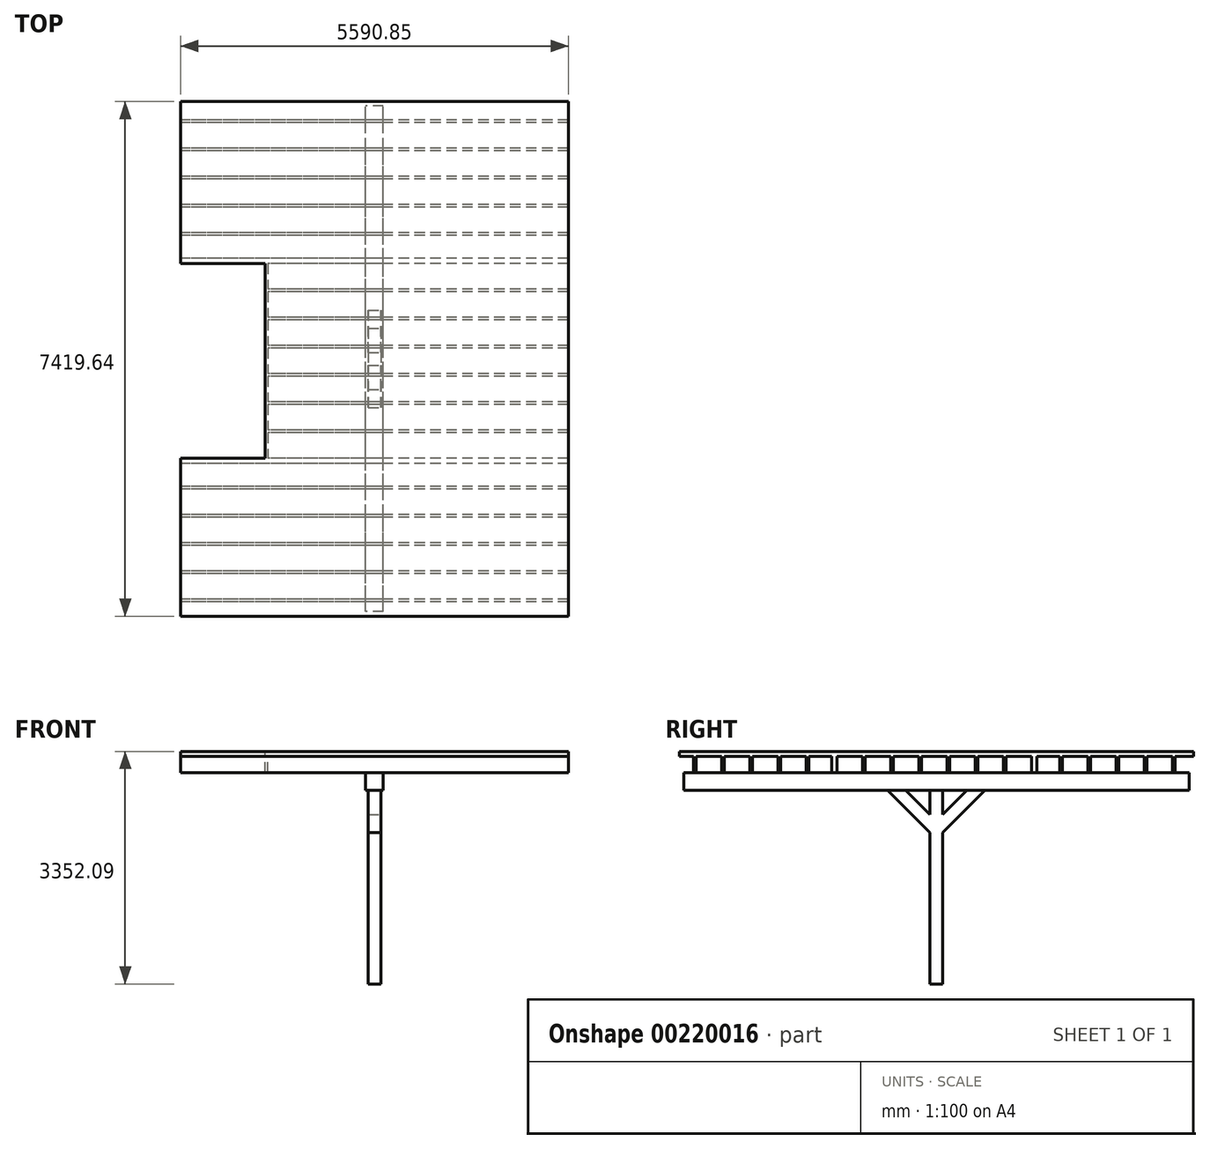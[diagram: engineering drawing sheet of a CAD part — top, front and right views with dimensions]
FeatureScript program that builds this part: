
annotation { "Feature Type Name" : "Feature", "Feature Type Description" : "" }
export const myFeature = defineFeature(function(context is Context, id is Id, definition is map)
    precondition{}
    {
        {
            var Q0;
            Q0=qCreatedBy(makeId("Top.planeOp"),FACE);
            var sketch = newSketch(context, id + "F0", { "sketchPlane" : qUnion([Q0])});
            skLineSegment(sketch, "E0.bottom", {"start": v(-4.2, 0) * mm, "end": v(5863.2, 0) * mm});
            skLineSegment(sketch, "E0.top", {"start": v(-4.2, -7696.2) * mm, "end": v(5863.2, -7696.2) * mm});
            skLineSegment(sketch, "E0.left", {"start": v(-4.2, 0) * mm, "end": v(-4.2, -7696.2) * mm});
            skLineSegment(sketch, "E0.right", {"start": v(5863.2, 0) * mm, "end": v(5863.2, -7696.2) * mm});
            skSolve(sketch);
        }
        {
            var Q0;
            Q0=makeQuery(id+"F0.imprint","IMPRINT",FACE,{"disambiguationData":[TD([[makeQuery(id+"F0.imprint","IMPRINT",EDGE,{"derivedFrom":sQuery(id+"F0.wireOp",EDGE,"E0.bottom")}),-1.0]])]});
            extrude(context, id + "F1", {"entities" : qUnion([Q0]), "depth" : 69.14 * mm});
        }
        {
            var Q0;
            Q0=makeQuery(id+"F1.opExtrude","CAP_FACE",FACE,{"disambiguationData":[OSD([sQuery(id+"F0.wireOp",EDGE,"E0.bottom"),sQuery(id+"F0.wireOp",EDGE,"E0.top"),sQuery(id+"F0.wireOp",EDGE,"E0.left"),sQuery(id+"F0.wireOp",EDGE,"E0.right")])],"isStart":true});
            var sketch = newSketch(context, id + "F2", { "sketchPlane" : qUnion([Q0])});
            skLineSegment(sketch, "E1.0", {"start": v(33.9, 7658.1) * mm, "end": v(5825.1, 7658.1) * mm});
            skLineSegment(sketch, "E1.1", {"start": v(33.9, 38.1) * mm, "end": v(33.9, 7658.1) * mm});
            skLineSegment(sketch, "E1.2", {"start": v(33.9, 38.1) * mm, "end": v(5825.1, 38.1) * mm});
            skLineSegment(sketch, "E1.3", {"start": v(5825.1, 38.1) * mm, "end": v(5825.1, 7658.1) * mm});
            skSolve(sketch);
        }
        {
            var Q0;
            Q0=makeQuery(id+"F2.imprint","IMPRINT",FACE,{"disambiguationData":[TD([[makeQuery(id+"F2.imprint","IMPRINT",EDGE,{"derivedFrom":sQuery(id+"F2.wireOp",EDGE,"E1.0")}),1.0]])]});
            extrude(context, id + "F3", {"entities" : qUnion([Q0]), "operationType" : NewBodyOperationType.ADD, "depth" : 234.95 * mm});
        }
        {
            var Q0;
            Q0=qCreatedBy(makeId("Right.planeOp"),FACE);
            var sketch = newSketch(context, id + "F4", { "sketchPlane" : qUnion([Q0])});
            skLineSegment(sketch, "E2.bottom", {"start": v(-406.4, 0) * mm, "end": v(-444.5, 0) * mm});
            skLineSegment(sketch, "E2.top", {"start": v(-406.4, -234.95) * mm, "end": v(-444.5, -234.95) * mm});
            skLineSegment(sketch, "E2.left", {"start": v(-406.4, 0) * mm, "end": v(-406.4, -234.95) * mm});
            skLineSegment(sketch, "E2.right", {"start": v(-444.5, 0) * mm, "end": v(-444.5, -234.95) * mm});
            skLineSegment(sketch, "E3.1.0.0", {"start": v(-812.8, 0) * mm, "end": v(-812.8, -234.95) * mm});
            skLineSegment(sketch, "E3.1.0.1", {"start": v(-850.9, 0) * mm, "end": v(-850.9, -234.95) * mm});
            skLineSegment(sketch, "E3.1.0.2", {"start": v(-812.8, 0) * mm, "end": v(-850.9, 0) * mm});
            skLineSegment(sketch, "E3.1.0.3", {"start": v(-812.8, -234.95) * mm, "end": v(-850.9, -234.95) * mm});
            skLineSegment(sketch, "E3.2.0.0", {"start": v(-1219.2, 0) * mm, "end": v(-1219.2, -234.95) * mm});
            skLineSegment(sketch, "E3.2.0.1", {"start": v(-1257.3, 0) * mm, "end": v(-1257.3, -234.95) * mm});
            skLineSegment(sketch, "E3.2.0.2", {"start": v(-1219.2, 0) * mm, "end": v(-1257.3, 0) * mm});
            skLineSegment(sketch, "E3.2.0.3", {"start": v(-1219.2, -234.95) * mm, "end": v(-1257.3, -234.95) * mm});
            skLineSegment(sketch, "E3.3.0.0", {"start": v(-1625.6, 0) * mm, "end": v(-1625.6, -234.95) * mm});
            skLineSegment(sketch, "E3.3.0.1", {"start": v(-1663.7, 0) * mm, "end": v(-1663.7, -234.95) * mm});
            skLineSegment(sketch, "E3.3.0.2", {"start": v(-1625.6, 0) * mm, "end": v(-1663.7, 0) * mm});
            skLineSegment(sketch, "E3.3.0.3", {"start": v(-1625.6, -234.95) * mm, "end": v(-1663.7, -234.95) * mm});
            skLineSegment(sketch, "E3.4.0.0", {"start": v(-2032, 0) * mm, "end": v(-2032, -234.95) * mm});
            skLineSegment(sketch, "E3.4.0.1", {"start": v(-2070.1, 0) * mm, "end": v(-2070.1, -234.95) * mm});
            skLineSegment(sketch, "E3.4.0.2", {"start": v(-2032, 0) * mm, "end": v(-2070.1, 0) * mm});
            skLineSegment(sketch, "E3.4.0.3", {"start": v(-2032, -234.95) * mm, "end": v(-2070.1, -234.95) * mm});
            skLineSegment(sketch, "E3.5.0.0", {"start": v(-2438.4, 0) * mm, "end": v(-2438.4, -234.95) * mm});
            skLineSegment(sketch, "E3.5.0.1", {"start": v(-2476.5, 0) * mm, "end": v(-2476.5, -234.95) * mm});
            skLineSegment(sketch, "E3.5.0.2", {"start": v(-2438.4, 0) * mm, "end": v(-2476.5, 0) * mm});
            skLineSegment(sketch, "E3.5.0.3", {"start": v(-2438.4, -234.95) * mm, "end": v(-2476.5, -234.95) * mm});
            skLineSegment(sketch, "E3.6.0.0", {"start": v(-2844.8, 0) * mm, "end": v(-2844.8, -234.95) * mm});
            skLineSegment(sketch, "E3.6.0.1", {"start": v(-2882.9, 0) * mm, "end": v(-2882.9, -234.95) * mm});
            skLineSegment(sketch, "E3.6.0.2", {"start": v(-2844.8, 0) * mm, "end": v(-2882.9, 0) * mm});
            skLineSegment(sketch, "E3.6.0.3", {"start": v(-2844.8, -234.95) * mm, "end": v(-2882.9, -234.95) * mm});
            skLineSegment(sketch, "E3.7.0.0", {"start": v(-3251.2, 0) * mm, "end": v(-3251.2, -234.95) * mm});
            skLineSegment(sketch, "E3.7.0.1", {"start": v(-3289.3, 0) * mm, "end": v(-3289.3, -234.95) * mm});
            skLineSegment(sketch, "E3.7.0.2", {"start": v(-3251.2, 0) * mm, "end": v(-3289.3, 0) * mm});
            skLineSegment(sketch, "E3.7.0.3", {"start": v(-3251.2, -234.95) * mm, "end": v(-3289.3, -234.95) * mm});
            skLineSegment(sketch, "E3.8.0.0", {"start": v(-3657.6, 0) * mm, "end": v(-3657.6, -234.95) * mm});
            skLineSegment(sketch, "E3.8.0.1", {"start": v(-3695.7, 0) * mm, "end": v(-3695.7, -234.95) * mm});
            skLineSegment(sketch, "E3.8.0.2", {"start": v(-3657.6, 0) * mm, "end": v(-3695.7, 0) * mm});
            skLineSegment(sketch, "E3.8.0.3", {"start": v(-3657.6, -234.95) * mm, "end": v(-3695.7, -234.95) * mm});
            skLineSegment(sketch, "E3.9.0.0", {"start": v(-4064, 0) * mm, "end": v(-4064, -234.95) * mm});
            skLineSegment(sketch, "E3.9.0.1", {"start": v(-4102.1, 0) * mm, "end": v(-4102.1, -234.95) * mm});
            skLineSegment(sketch, "E3.9.0.2", {"start": v(-4064, 0) * mm, "end": v(-4102.1, 0) * mm});
            skLineSegment(sketch, "E3.9.0.3", {"start": v(-4064, -234.95) * mm, "end": v(-4102.1, -234.95) * mm});
            skLineSegment(sketch, "E3.10.0.0", {"start": v(-4470.4, 0) * mm, "end": v(-4470.4, -234.95) * mm});
            skLineSegment(sketch, "E3.10.0.1", {"start": v(-4508.5, 0) * mm, "end": v(-4508.5, -234.95) * mm});
            skLineSegment(sketch, "E3.10.0.2", {"start": v(-4470.4, 0) * mm, "end": v(-4508.5, 0) * mm});
            skLineSegment(sketch, "E3.10.0.3", {"start": v(-4470.4, -234.95) * mm, "end": v(-4508.5, -234.95) * mm});
            skLineSegment(sketch, "E3.11.0.0", {"start": v(-4876.8, 0) * mm, "end": v(-4876.8, -234.95) * mm});
            skLineSegment(sketch, "E3.11.0.1", {"start": v(-4914.9, 0) * mm, "end": v(-4914.9, -234.95) * mm});
            skLineSegment(sketch, "E3.11.0.2", {"start": v(-4876.8, 0) * mm, "end": v(-4914.9, 0) * mm});
            skLineSegment(sketch, "E3.11.0.3", {"start": v(-4876.8, -234.95) * mm, "end": v(-4914.9, -234.95) * mm});
            skLineSegment(sketch, "E3.12.0.0", {"start": v(-5283.2, 0) * mm, "end": v(-5283.2, -234.95) * mm});
            skLineSegment(sketch, "E3.12.0.1", {"start": v(-5321.3, 0) * mm, "end": v(-5321.3, -234.95) * mm});
            skLineSegment(sketch, "E3.12.0.2", {"start": v(-5283.2, 0) * mm, "end": v(-5321.3, 0) * mm});
            skLineSegment(sketch, "E3.12.0.3", {"start": v(-5283.2, -234.95) * mm, "end": v(-5321.3, -234.95) * mm});
            skLineSegment(sketch, "E3.13.0.0", {"start": v(-5689.6, 0) * mm, "end": v(-5689.6, -234.95) * mm});
            skLineSegment(sketch, "E3.13.0.1", {"start": v(-5727.7, 0) * mm, "end": v(-5727.7, -234.95) * mm});
            skLineSegment(sketch, "E3.13.0.2", {"start": v(-5689.6, 0) * mm, "end": v(-5727.7, 0) * mm});
            skLineSegment(sketch, "E3.13.0.3", {"start": v(-5689.6, -234.95) * mm, "end": v(-5727.7, -234.95) * mm});
            skLineSegment(sketch, "E3.14.0.0", {"start": v(-6096, 0) * mm, "end": v(-6096, -234.95) * mm});
            skLineSegment(sketch, "E3.14.0.1", {"start": v(-6134.1, 0) * mm, "end": v(-6134.1, -234.95) * mm});
            skLineSegment(sketch, "E3.14.0.2", {"start": v(-6096, 0) * mm, "end": v(-6134.1, 0) * mm});
            skLineSegment(sketch, "E3.14.0.3", {"start": v(-6096, -234.95) * mm, "end": v(-6134.1, -234.95) * mm});
            skLineSegment(sketch, "E3.15.0.0", {"start": v(-6502.4, 0) * mm, "end": v(-6502.4, -234.95) * mm});
            skLineSegment(sketch, "E3.15.0.1", {"start": v(-6540.5, 0) * mm, "end": v(-6540.5, -234.95) * mm});
            skLineSegment(sketch, "E3.15.0.2", {"start": v(-6502.4, 0) * mm, "end": v(-6540.5, 0) * mm});
            skLineSegment(sketch, "E3.15.0.3", {"start": v(-6502.4, -234.95) * mm, "end": v(-6540.5, -234.95) * mm});
            skLineSegment(sketch, "E3.16.0.0", {"start": v(-6908.8, 0) * mm, "end": v(-6908.8, -234.95) * mm});
            skLineSegment(sketch, "E3.16.0.1", {"start": v(-6946.9, 0) * mm, "end": v(-6946.9, -234.95) * mm});
            skLineSegment(sketch, "E3.16.0.2", {"start": v(-6908.8, 0) * mm, "end": v(-6946.9, 0) * mm});
            skLineSegment(sketch, "E3.16.0.3", {"start": v(-6908.8, -234.95) * mm, "end": v(-6946.9, -234.95) * mm});
            skLineSegment(sketch, "E3.direction1", {"start": v(-444.5, -234.95) * mm, "end": v(-850.9, -234.95) * mm, "construction": true});
            skLineSegment(sketch, "E4.0.17.0", {"start": v(-7315.2, 0) * mm, "end": v(-7315.2, -234.95) * mm});
            skLineSegment(sketch, "E4.3.17.0", {"start": v(-7353.3, 0) * mm, "end": v(-7353.3, -234.95) * mm});
            skLineSegment(sketch, "E4.6.17.0", {"start": v(-7315.2, 0) * mm, "end": v(-7353.3, 0) * mm});
            skLineSegment(sketch, "E4.9.17.0", {"start": v(-7315.2, -234.95) * mm, "end": v(-7353.3, -234.95) * mm});
            skSolve(sketch);
        }
        {
            var Q0;
            Q0=makeQuery(id+"F4.imprint","IMPRINT",FACE,{"disambiguationData":[TD([[makeQuery(id+"F4.imprint","IMPRINT",EDGE,{"derivedFrom":sQuery(id+"F4.wireOp",EDGE,"E2.bottom")}),1.0]])]});
            var Q1;
            Q1=makeQuery(id+"F4.imprint","IMPRINT",FACE,{"disambiguationData":[TD([[makeQuery(id+"F4.imprint","IMPRINT",EDGE,{"derivedFrom":sQuery(id+"F4.wireOp",EDGE,"E3.1.0.0")}),-1.0]])]});
            var Q2;
            Q2=makeQuery(id+"F4.imprint","IMPRINT",FACE,{"disambiguationData":[TD([[makeQuery(id+"F4.imprint","IMPRINT",EDGE,{"derivedFrom":sQuery(id+"F4.wireOp",EDGE,"E3.2.0.0")}),-1.0]])]});
            var Q3;
            Q3=makeQuery(id+"F4.imprint","IMPRINT",FACE,{"disambiguationData":[TD([[makeQuery(id+"F4.imprint","IMPRINT",EDGE,{"derivedFrom":sQuery(id+"F4.wireOp",EDGE,"E3.3.0.0")}),-1.0]])]});
            var Q4;
            Q4=makeQuery(id+"F4.imprint","IMPRINT",FACE,{"disambiguationData":[TD([[makeQuery(id+"F4.imprint","IMPRINT",EDGE,{"derivedFrom":sQuery(id+"F4.wireOp",EDGE,"E3.4.0.0")}),-1.0]])]});
            var Q5;
            Q5=makeQuery(id+"F4.imprint","IMPRINT",FACE,{"disambiguationData":[TD([[makeQuery(id+"F4.imprint","IMPRINT",EDGE,{"derivedFrom":sQuery(id+"F4.wireOp",EDGE,"E3.5.0.0")}),-1.0]])]});
            var Q6;
            Q6=makeQuery(id+"F4.imprint","IMPRINT",FACE,{"disambiguationData":[TD([[makeQuery(id+"F4.imprint","IMPRINT",EDGE,{"derivedFrom":sQuery(id+"F4.wireOp",EDGE,"E3.6.0.0")}),-1.0]])]});
            var Q7;
            Q7=makeQuery(id+"F4.imprint","IMPRINT",FACE,{"disambiguationData":[TD([[makeQuery(id+"F4.imprint","IMPRINT",EDGE,{"derivedFrom":sQuery(id+"F4.wireOp",EDGE,"E3.7.0.0")}),-1.0]])]});
            var Q8;
            Q8=makeQuery(id+"F4.imprint","IMPRINT",FACE,{"disambiguationData":[TD([[makeQuery(id+"F4.imprint","IMPRINT",EDGE,{"derivedFrom":sQuery(id+"F4.wireOp",EDGE,"E3.8.0.0")}),-1.0]])]});
            var Q9;
            Q9=makeQuery(id+"F4.imprint","IMPRINT",FACE,{"disambiguationData":[TD([[makeQuery(id+"F4.imprint","IMPRINT",EDGE,{"derivedFrom":sQuery(id+"F4.wireOp",EDGE,"E3.9.0.0")}),-1.0]])]});
            var Q10;
            Q10=makeQuery(id+"F4.imprint","IMPRINT",FACE,{"disambiguationData":[TD([[makeQuery(id+"F4.imprint","IMPRINT",EDGE,{"derivedFrom":sQuery(id+"F4.wireOp",EDGE,"E3.10.0.0")}),-1.0]])]});
            var Q11;
            Q11=makeQuery(id+"F4.imprint","IMPRINT",FACE,{"disambiguationData":[TD([[makeQuery(id+"F4.imprint","IMPRINT",EDGE,{"derivedFrom":sQuery(id+"F4.wireOp",EDGE,"E3.11.0.0")}),-1.0]])]});
            var Q12;
            Q12=makeQuery(id+"F4.imprint","IMPRINT",FACE,{"disambiguationData":[TD([[makeQuery(id+"F4.imprint","IMPRINT",EDGE,{"derivedFrom":sQuery(id+"F4.wireOp",EDGE,"E3.12.0.0")}),-1.0]])]});
            var Q13;
            Q13=makeQuery(id+"F4.imprint","IMPRINT",FACE,{"disambiguationData":[TD([[makeQuery(id+"F4.imprint","IMPRINT",EDGE,{"derivedFrom":sQuery(id+"F4.wireOp",EDGE,"E3.13.0.0")}),-1.0]])]});
            var Q14;
            Q14=makeQuery(id+"F4.imprint","IMPRINT",FACE,{"disambiguationData":[TD([[makeQuery(id+"F4.imprint","IMPRINT",EDGE,{"derivedFrom":sQuery(id+"F4.wireOp",EDGE,"E3.14.0.0")}),-1.0]])]});
            var Q15;
            Q15=makeQuery(id+"F4.imprint","IMPRINT",FACE,{"disambiguationData":[TD([[makeQuery(id+"F4.imprint","IMPRINT",EDGE,{"derivedFrom":sQuery(id+"F4.wireOp",EDGE,"E3.15.0.0")}),-1.0]])]});
            var Q16;
            Q16=makeQuery(id+"F4.imprint","IMPRINT",FACE,{"disambiguationData":[TD([[makeQuery(id+"F4.imprint","IMPRINT",EDGE,{"derivedFrom":sQuery(id+"F4.wireOp",EDGE,"E3.16.0.0")}),-1.0]])]});
            var Q17;
            Q17=makeQuery(id+"F4.imprint","IMPRINT",FACE,{"disambiguationData":[TD([[makeQuery(id+"F4.imprint","IMPRINT",EDGE,{"derivedFrom":sQuery(id+"F4.wireOp",EDGE,"E4.0.17.0")}),-1.0]])]});
            var Q18;
            Q18=makeQuery(id+"F1.opExtrude","SWEPT_FACE",FACE,{"disambiguationData":[OSD([sQuery(id+"F0.wireOp",EDGE,"E0.right")])]});
            extrude(context, id + "F5", {"entities" : qUnion([Q0, Q1, Q2, Q3, Q4, Q5, Q6, Q7, Q8, Q9, Q10, Q11, Q12, Q13, Q14, Q15, Q16, Q17]), "operationType" : NewBodyOperationType.ADD, "endBound" : BoundingType.UP_TO_SURFACE, "endBoundEntityFace" : qUnion([Q18]), "depth" : 25.4 * mm});
        }
        {
            var Q0;
            {var subQ0=sQuery(id+"F0.wireOp",EDGE,"E0.bottom");Q0=makeQuery(id+"F3.boolean.opBoolean","MERGE",FACE,{"derivedFrom":[makeQuery(id+"F1.opExtrude","SWEPT_FACE",FACE,{"disambiguationData":[OSD([subQ0])]}),makeQuery(id+"F3.opExtrude","SWEPT_FACE",FACE,{"disambiguationData":[OSD([subQ0])]})]});}
            cPlane(context, id + "F6", {"entities" : qUnion([Q0]), "cplaneType" : CPlaneType.OFFSET, "offset" : 203.2 * mm, "oppositeDirection" : true, "width" : 152.4 * mm, "height" : 152.4 * mm});
        }
        {
            var Q0;
            Q0=qCreatedBy(id+"F6.planeOp",FACE);
            var sketch = newSketch(context, id + "F7", { "sketchPlane" : qUnion([Q0])});
            skLineSegment(sketch, "E5.bottom", {"start": v(-3056.5, -234.95) * mm, "end": v(-2802.5, -234.95) * mm});
            skLineSegment(sketch, "E5.top", {"start": v(-3056.5, -488.95) * mm, "end": v(-2802.5, -488.95) * mm});
            skLineSegment(sketch, "E5.left", {"start": v(-3056.5, -234.95) * mm, "end": v(-3056.5, -488.95) * mm});
            skLineSegment(sketch, "E5.right", {"start": v(-2802.5, -234.95) * mm, "end": v(-2802.5, -488.95) * mm});
            skSolve(sketch);
        }
        {
            var Q0;
            Q0=makeQuery(id+"F7.imprint","IMPRINT",FACE,{"disambiguationData":[TD([[makeQuery(id+"F7.imprint","IMPRINT",EDGE,{"derivedFrom":sQuery(id+"F7.wireOp",EDGE,"E5.bottom")}),-1.0]])]});
            extrude(context, id + "F8", {"entities" : qUnion([Q0]), "operationType" : NewBodyOperationType.ADD, "oppositeDirection" : true, "depth" : 7289.8 * mm});
        }
        {
            var Q0;
            Q0=makeQuery(id+"F8.opExtrude","SWEPT_FACE",FACE,{"disambiguationData":[OSD([sQuery(id+"F7.wireOp",EDGE,"E5.top")])]});
            var sketch = newSketch(context, id + "F9", { "sketchPlane" : qUnion([Q0])});
            skLineSegment(sketch, "E6", {"start": v(2929.5, 7493) * mm, "end": v(2929.5, 203.2) * mm, "construction": true});
            skLineSegment(sketch, "E7", {"start": v(2802.5, 3848.1) * mm, "end": v(3056.5, 3848.1) * mm, "construction": true});
            skLineSegment(sketch, "E8.bottom", {"start": v(3021.58, 3756.03) * mm, "end": v(2837.43, 3756.03) * mm});
            skLineSegment(sketch, "E8.top", {"start": v(3021.58, 3940.18) * mm, "end": v(2837.43, 3940.18) * mm});
            skLineSegment(sketch, "E8.left", {"start": v(3021.58, 3756.03) * mm, "end": v(3021.58, 3940.18) * mm});
            skLineSegment(sketch, "E8.right", {"start": v(2837.43, 3756.03) * mm, "end": v(2837.43, 3940.18) * mm});
            skPoint(sketch, "E8.middle", {"position": v(2929.5, 3848.1) * mm});
            skSolve(sketch);
        }
        {
            var Q0;
            Q0=makeQuery(id+"F9.imprint","IMPRINT",FACE,{"disambiguationData":[TD([[makeQuery(id+"F9.imprint","IMPRINT",EDGE,{"derivedFrom":sQuery(id+"F9.wireOp",EDGE,"E8.bottom")}),-1.0]])]});
            extrude(context, id + "F10", {"entities" : qUnion([Q0]), "operationType" : NewBodyOperationType.ADD, "depth" : 2794 * mm});
        }
        {
            var Q0;
            Q0=makeQuery(id+"F10.opExtrude","SWEPT_FACE",FACE,{"disambiguationData":[OSD([sQuery(id+"F9.wireOp",EDGE,"E8.left")])]});
            var sketch = newSketch(context, id + "F11", { "sketchPlane" : qUnion([Q0])});
            skLineSegment(sketch, "E9", {"start": v(-4289.35, -488.95) * mm, "end": v(-3940.17, -838.12) * mm});
            skLineSegment(sketch, "E10", {"start": v(-3940.17, -838.12) * mm, "end": v(-3940.17, -1098.55) * mm});
            skLineSegment(sketch, "E11", {"start": v(-3940.17, -1098.55) * mm, "end": v(-4549.77, -488.95) * mm});
            skLineSegment(sketch, "E12", {"start": v(-4549.77, -488.95) * mm, "end": v(-4289.35, -488.95) * mm});
            skLineSegment(sketch, "E13", {"start": v(-3848.1, -488.95) * mm, "end": v(-3848.1, -1270.1) * mm, "construction": true});
            skLineSegment(sketch, "E14.MirrorCS", {"start": v(-3146.42, -488.95) * mm, "end": v(-3406.85, -488.95) * mm});
            skLineSegment(sketch, "E15.MirrorCS", {"start": v(-3756.02, -1098.55) * mm, "end": v(-3146.42, -488.95) * mm});
            skLineSegment(sketch, "E16.MirrorCS", {"start": v(-3406.85, -488.95) * mm, "end": v(-3756.02, -838.12) * mm});
            skLineSegment(sketch, "E17.MirrorCS", {"start": v(-3756.02, -838.12) * mm, "end": v(-3756.02, -1098.55) * mm});
            skSolve(sketch);
        }
        {
            var Q0;
            Q0=makeQuery(id+"F11.imprint","IMPRINT",FACE,{"disambiguationData":[TD([[makeQuery(id+"F11.imprint","IMPRINT",EDGE,{"derivedFrom":sQuery(id+"F11.wireOp",EDGE,"E9")}),-1.0]])]});
            var Q1;
            Q1=makeQuery(id+"F11.imprint","IMPRINT",FACE,{"disambiguationData":[TD([[makeQuery(id+"F11.imprint","IMPRINT",EDGE,{"derivedFrom":sQuery(id+"F11.wireOp",EDGE,"E14.MirrorCS")}),1.0]])]});
            var Q2;
            Q2=makeQuery(id+"F10.opExtrude","SWEPT_FACE",FACE,{"disambiguationData":[OSD([sQuery(id+"F9.wireOp",EDGE,"E8.right")])]});
            extrude(context, id + "F12", {"entities" : qUnion([Q0, Q1]), "operationType" : NewBodyOperationType.ADD, "endBound" : BoundingType.UP_TO_SURFACE, "oppositeDirection" : true, "endBoundEntityFace" : qUnion([Q2]), "depth" : 25.4 * mm});
        }
        {
            var Q0;
            Q0=makeQuery(id+"F1.opExtrude","CAP_FACE",FACE,{"disambiguationData":[OSD([sQuery(id+"F0.wireOp",EDGE,"E0.bottom"),sQuery(id+"F0.wireOp",EDGE,"E0.top"),sQuery(id+"F0.wireOp",EDGE,"E0.left"),sQuery(id+"F0.wireOp",EDGE,"E0.right")])],"isStart":false});
            var sketch = newSketch(context, id + "F13", { "sketchPlane" : qUnion([Q0])});
            skLineSegment(sketch, "E18.0", {"start": v(134.08, -138.28) * mm, "end": v(5724.93, -138.28) * mm});
            skLineSegment(sketch, "E18.1", {"start": v(134.08, -138.28) * mm, "end": v(134.08, -7557.92) * mm});
            skLineSegment(sketch, "E18.2", {"start": v(134.08, -7557.92) * mm, "end": v(5724.93, -7557.92) * mm});
            skLineSegment(sketch, "E18.3", {"start": v(5724.93, -138.28) * mm, "end": v(5724.93, -7557.92) * mm});
            skLineSegment(sketch, "E19.0", {"start": v(-4.2, 0) * mm, "end": v(5863.2, 0) * mm});
            skLineSegment(sketch, "E20.0", {"start": v(-4.2, 0) * mm, "end": v(-4.2, -7696.2) * mm});
            skLineSegment(sketch, "E21.0", {"start": v(-4.2, -7696.2) * mm, "end": v(5863.2, -7696.2) * mm});
            skLineSegment(sketch, "E22.0", {"start": v(5863.2, 0) * mm, "end": v(5863.2, -7696.2) * mm});
            skSolve(sketch);
        }
        {
            var Q0;
            Q0=makeQuery(id+"F13.imprint","IMPRINT",FACE,{"disambiguationData":[TD([[makeQuery(id+"F13.imprint","IMPRINT",EDGE,{"derivedFrom":sQuery(id+"F13.wireOp",EDGE,"E18.0")}),1.0]])]});
            var Q1;
            Q1=makeQuery(id+"F5.boolean.opBoolean","MERGE",FACE,{"derivedFrom":[makeQuery(id+"F3.opExtrude","CAP_FACE",FACE,{"disambiguationData":[OSD([sQuery(id+"F0.wireOp",EDGE,"E0.bottom"),sQuery(id+"F0.wireOp",EDGE,"E0.top"),sQuery(id+"F0.wireOp",EDGE,"E0.left"),sQuery(id+"F0.wireOp",EDGE,"E0.right"),sQuery(id+"F2.wireOp",EDGE,"E1.0"),sQuery(id+"F2.wireOp",EDGE,"E1.1"),sQuery(id+"F2.wireOp",EDGE,"E1.2"),sQuery(id+"F2.wireOp",EDGE,"E1.3")])],"isStart":false}),makeQuery(id+"F5.opExtrude","SWEPT_FACE",FACE,{"disambiguationData":[OSD([sQuery(id+"F4.wireOp",EDGE,"E2.top")])]}),makeQuery(id+"F5.opExtrude","SWEPT_FACE",FACE,{"disambiguationData":[OSD([sQuery(id+"F4.wireOp",EDGE,"E3.1.0.3")])]}),makeQuery(id+"F5.opExtrude","SWEPT_FACE",FACE,{"disambiguationData":[OSD([sQuery(id+"F4.wireOp",EDGE,"E3.2.0.3")])]}),makeQuery(id+"F5.opExtrude","SWEPT_FACE",FACE,{"disambiguationData":[OSD([sQuery(id+"F4.wireOp",EDGE,"E3.3.0.3")])]}),makeQuery(id+"F5.opExtrude","SWEPT_FACE",FACE,{"disambiguationData":[OSD([sQuery(id+"F4.wireOp",EDGE,"E3.4.0.3")])]}),makeQuery(id+"F5.opExtrude","SWEPT_FACE",FACE,{"disambiguationData":[OSD([sQuery(id+"F4.wireOp",EDGE,"E3.5.0.3")])]}),makeQuery(id+"F5.opExtrude","SWEPT_FACE",FACE,{"disambiguationData":[OSD([sQuery(id+"F4.wireOp",EDGE,"E3.6.0.3")])]}),makeQuery(id+"F5.opExtrude","SWEPT_FACE",FACE,{"disambiguationData":[OSD([sQuery(id+"F4.wireOp",EDGE,"E3.7.0.3")])]}),makeQuery(id+"F5.opExtrude","SWEPT_FACE",FACE,{"disambiguationData":[OSD([sQuery(id+"F4.wireOp",EDGE,"E3.8.0.3")])]}),makeQuery(id+"F5.opExtrude","SWEPT_FACE",FACE,{"disambiguationData":[OSD([sQuery(id+"F4.wireOp",EDGE,"E3.9.0.3")])]}),makeQuery(id+"F5.opExtrude","SWEPT_FACE",FACE,{"disambiguationData":[OSD([sQuery(id+"F4.wireOp",EDGE,"E3.10.0.3")])]}),makeQuery(id+"F5.opExtrude","SWEPT_FACE",FACE,{"disambiguationData":[OSD([sQuery(id+"F4.wireOp",EDGE,"E3.11.0.3")])]}),makeQuery(id+"F5.opExtrude","SWEPT_FACE",FACE,{"disambiguationData":[OSD([sQuery(id+"F4.wireOp",EDGE,"E3.12.0.3")])]}),makeQuery(id+"F5.opExtrude","SWEPT_FACE",FACE,{"disambiguationData":[OSD([sQuery(id+"F4.wireOp",EDGE,"E3.13.0.3")])]}),makeQuery(id+"F5.opExtrude","SWEPT_FACE",FACE,{"disambiguationData":[OSD([sQuery(id+"F4.wireOp",EDGE,"E3.14.0.3")])]}),makeQuery(id+"F5.opExtrude","SWEPT_FACE",FACE,{"disambiguationData":[OSD([sQuery(id+"F4.wireOp",EDGE,"E3.15.0.3")])]}),makeQuery(id+"F5.opExtrude","SWEPT_FACE",FACE,{"disambiguationData":[OSD([sQuery(id+"F4.wireOp",EDGE,"E3.16.0.3")])]}),makeQuery(id+"F5.opExtrude","SWEPT_FACE",FACE,{"disambiguationData":[OSD([sQuery(id+"F4.wireOp",EDGE,"E4.9.17.0")])]})]});
            extrude(context, id + "F14", {"entities" : qUnion([Q0]), "operationType" : NewBodyOperationType.REMOVE, "endBound" : BoundingType.UP_TO_SURFACE, "oppositeDirection" : true, "endBoundEntityFace" : qUnion([Q1]), "depth" : 25.4 * mm});
        }
        {
            var Q0;
            Q0=makeQuery(id+"F1.opExtrude","CAP_FACE",FACE,{"disambiguationData":[OSD([sQuery(id+"F0.wireOp",EDGE,"E0.bottom"),sQuery(id+"F0.wireOp",EDGE,"E0.top"),sQuery(id+"F0.wireOp",EDGE,"E0.left"),sQuery(id+"F0.wireOp",EDGE,"E0.right")])],"isStart":false});
            var sketch = newSketch(context, id + "F15", { "sketchPlane" : qUnion([Q0])});
            skLineSegment(sketch, "E23.bottom", {"start": v(134.08, -2476.5) * mm, "end": v(1353.28, -2476.5) * mm});
            skLineSegment(sketch, "E23.top", {"start": v(134.08, -5283.2) * mm, "end": v(1353.28, -5283.2) * mm});
            skLineSegment(sketch, "E23.left", {"start": v(134.08, -2476.5) * mm, "end": v(134.08, -5283.2) * mm});
            skLineSegment(sketch, "E23.right", {"start": v(1353.28, -2476.5) * mm, "end": v(1353.28, -5283.2) * mm});
            skSolve(sketch);
        }
        {
            var Q0;
            Q0=makeQuery(id+"F15.imprint","IMPRINT",FACE,{"disambiguationData":[TD([[makeQuery(id+"F15.imprint","IMPRINT",EDGE,{"derivedFrom":sQuery(id+"F15.wireOp",EDGE,"E23.bottom")}),-1.0]])]});
            extrude(context, id + "F16", {"entities" : qUnion([Q0]), "operationType" : NewBodyOperationType.REMOVE, "oppositeDirection" : true, "depth" : 304.8 * mm});
        }
        {
            var Q0;
            Q0=makeQuery(id+"F16.boolean.opBoolean","COPY",FACE,{"derivedFrom":makeQuery(id+"F16.opExtrude","SWEPT_FACE",FACE,{"disambiguationData":[OSD([sQuery(id+"F15.wireOp",EDGE,"E23.right")])]})});
            var sketch = newSketch(context, id + "F17", { "sketchPlane" : qUnion([Q0])});
            skLineSegment(sketch, "E24.bottom", {"start": v(2476.5, 0) * mm, "end": v(5283.2, 0) * mm});
            skLineSegment(sketch, "E24.top", {"start": v(2476.5, -234.95) * mm, "end": v(5283.2, -234.95) * mm});
            skLineSegment(sketch, "E24.left", {"start": v(2476.5, 0) * mm, "end": v(2476.5, -234.95) * mm});
            skLineSegment(sketch, "E24.right", {"start": v(5283.2, 0) * mm, "end": v(5283.2, -234.95) * mm});
            skSolve(sketch);
        }
        {
            var Q0;
            {var subQ0=sQuery(id+"F17.wireOp",EDGE,"E24.left");Q0=makeQuery(id+"F17.imprint","IMPRINT",FACE,{"disambiguationData":[TD([[makeQuery(id+"F17.imprint","IMPRINT",EDGE,{"derivedFrom":subQ0}),1.0]])]});}
            var Q1;
            {var subQ1=makeQuery(id+"F16.opExtrude","SWEPT_FACE",FACE,{"disambiguationData":[OSD([sQuery(id+"F15.wireOp",EDGE,"E23.right")])]});var subQ2=makeQuery(id+"F16.boolean.opBoolean","INTERSECT",EDGE,{"derivedFrom":[makeQuery(id+"F5.opExtrude","SWEPT_FACE",FACE,{"disambiguationData":[OSD([sQuery(id+"F4.wireOp",EDGE,"E3.6.0.1")])]}),subQ1]});Q1=makeQuery(id+"F17.imprint","IMPRINT",FACE,{"disambiguationData":[TD([[makeQuery(id+"F17.imprint","IMPRINT",EDGE,{"derivedFrom":subQ2}),-1.0]])]});}
            var Q2;
            {var subQ1=makeQuery(id+"F16.opExtrude","SWEPT_FACE",FACE,{"disambiguationData":[OSD([sQuery(id+"F15.wireOp",EDGE,"E23.right")])]});var subQ2=makeQuery(id+"F16.boolean.opBoolean","INTERSECT",EDGE,{"derivedFrom":[makeQuery(id+"F5.opExtrude","SWEPT_FACE",FACE,{"disambiguationData":[OSD([sQuery(id+"F4.wireOp",EDGE,"E3.7.0.1")])]}),subQ1]});Q2=makeQuery(id+"F17.imprint","IMPRINT",FACE,{"disambiguationData":[TD([[makeQuery(id+"F17.imprint","IMPRINT",EDGE,{"derivedFrom":subQ2}),-1.0]])]});}
            var Q3;
            {var subQ1=makeQuery(id+"F16.opExtrude","SWEPT_FACE",FACE,{"disambiguationData":[OSD([sQuery(id+"F15.wireOp",EDGE,"E23.right")])]});var subQ2=makeQuery(id+"F16.boolean.opBoolean","INTERSECT",EDGE,{"derivedFrom":[makeQuery(id+"F5.opExtrude","SWEPT_FACE",FACE,{"disambiguationData":[OSD([sQuery(id+"F4.wireOp",EDGE,"E3.8.0.1")])]}),subQ1]});Q3=makeQuery(id+"F17.imprint","IMPRINT",FACE,{"disambiguationData":[TD([[makeQuery(id+"F17.imprint","IMPRINT",EDGE,{"derivedFrom":subQ2}),-1.0]])]});}
            var Q4;
            {var subQ1=makeQuery(id+"F16.opExtrude","SWEPT_FACE",FACE,{"disambiguationData":[OSD([sQuery(id+"F15.wireOp",EDGE,"E23.right")])]});var subQ2=makeQuery(id+"F16.boolean.opBoolean","INTERSECT",EDGE,{"derivedFrom":[makeQuery(id+"F5.opExtrude","SWEPT_FACE",FACE,{"disambiguationData":[OSD([sQuery(id+"F4.wireOp",EDGE,"E3.9.0.1")])]}),subQ1]});Q4=makeQuery(id+"F17.imprint","IMPRINT",FACE,{"disambiguationData":[TD([[makeQuery(id+"F17.imprint","IMPRINT",EDGE,{"derivedFrom":subQ2}),-1.0]])]});}
            var Q5;
            {var subQ1=makeQuery(id+"F16.opExtrude","SWEPT_FACE",FACE,{"disambiguationData":[OSD([sQuery(id+"F15.wireOp",EDGE,"E23.right")])]});var subQ2=makeQuery(id+"F16.boolean.opBoolean","INTERSECT",EDGE,{"derivedFrom":[makeQuery(id+"F5.opExtrude","SWEPT_FACE",FACE,{"disambiguationData":[OSD([sQuery(id+"F4.wireOp",EDGE,"E3.10.0.1")])]}),subQ1]});Q5=makeQuery(id+"F17.imprint","IMPRINT",FACE,{"disambiguationData":[TD([[makeQuery(id+"F17.imprint","IMPRINT",EDGE,{"derivedFrom":subQ2}),-1.0]])]});}
            var Q6;
            {var subQ0=sQuery(id+"F17.wireOp",EDGE,"E24.right");Q6=makeQuery(id+"F17.imprint","IMPRINT",FACE,{"disambiguationData":[TD([[makeQuery(id+"F17.imprint","IMPRINT",EDGE,{"derivedFrom":subQ0}),-1.0]])]});}
            extrude(context, id + "F18", {"entities" : qUnion([Q0, Q1, Q2, Q3, Q4, Q5, Q6]), "operationType" : NewBodyOperationType.ADD, "oppositeDirection" : true, "depth" : 38.1 * mm});
        }
        {
            var Q0;
            Q0=makeQuery(id+"F5.opExtrude","SWEPT_FACE",FACE,{"disambiguationData":[OSD([sQuery(id+"F4.wireOp",EDGE,"E3.12.0.1")])]});
            extrude(context, id + "F19", {"entities" : qUnion([Q0]), "operationType" : NewBodyOperationType.ADD, "depth" : 38.1 * mm});
        }
        {
            var Q0;
            Q0=makeQuery(id+"F5.opExtrude","SWEPT_FACE",FACE,{"disambiguationData":[OSD([sQuery(id+"F4.wireOp",EDGE,"E3.5.0.0")])]});
            extrude(context, id + "F20", {"entities" : qUnion([Q0]), "operationType" : NewBodyOperationType.ADD, "depth" : 38.1 * mm});
        }
    });
